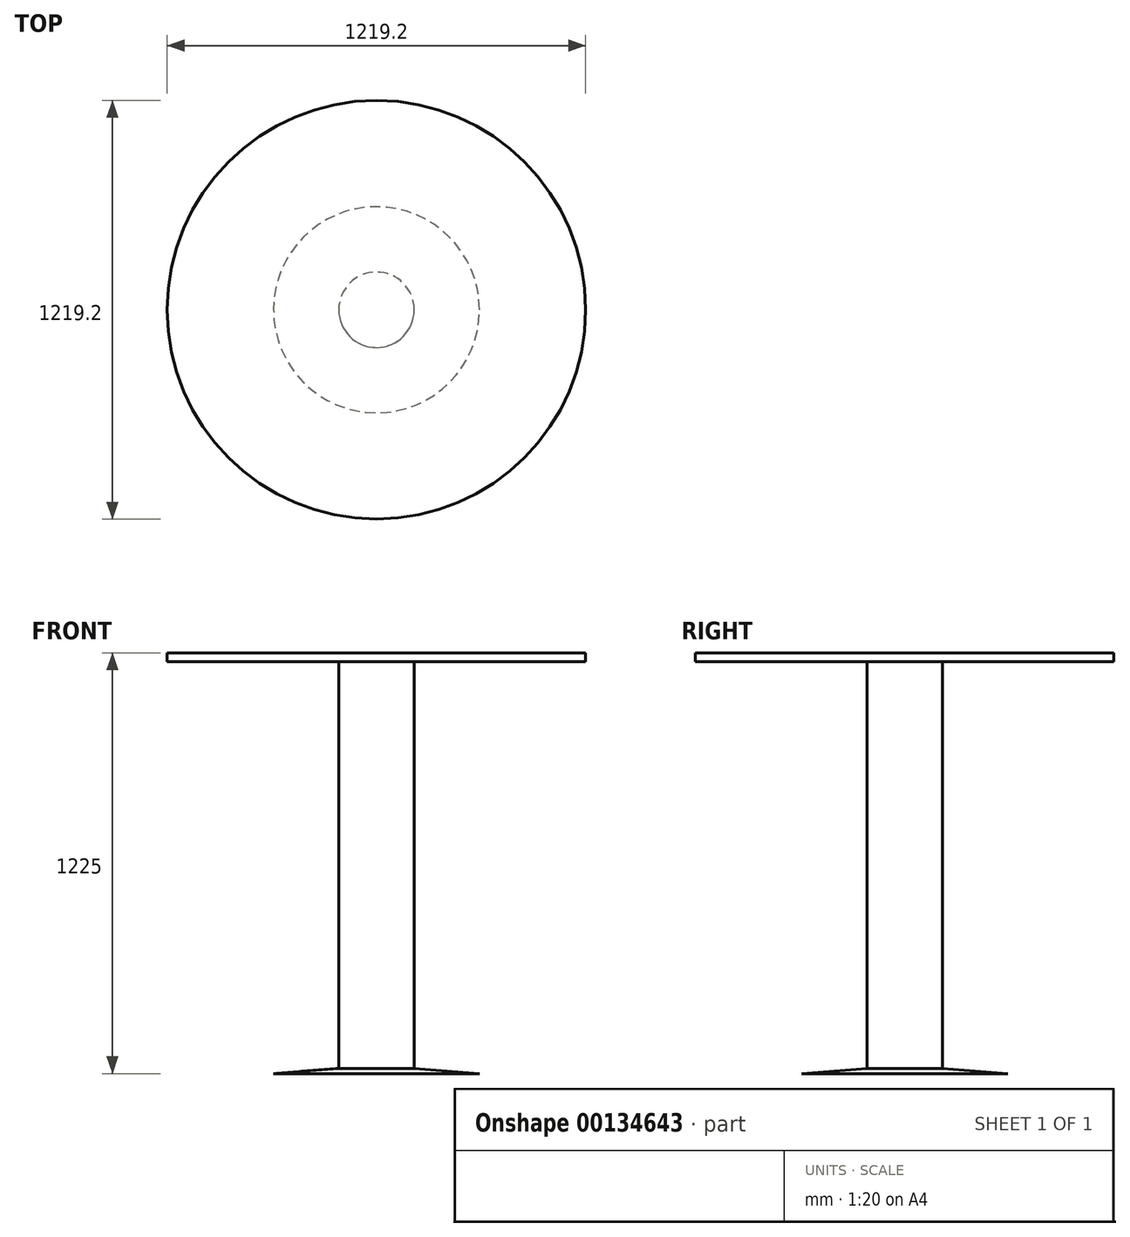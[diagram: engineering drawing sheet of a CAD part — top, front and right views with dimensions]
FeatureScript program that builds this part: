
annotation { "Feature Type Name" : "Feature", "Feature Type Description" : "" }
export const myFeature = defineFeature(function(context is Context, id is Id, definition is map)
    precondition{}
    {
        {
            var Q0;
            Q0=qCreatedBy(makeId("Top.planeOp"),FACE);
            var sketch = newSketch(context, id + "F0", { "sketchPlane" : qUnion([Q0])});
            skCircle(sketch, "E0", {"center": v(0, 0) * mm, "radius": 110 * mm});
            skSolve(sketch);
        }
        {
            var Q0;
            Q0=makeQuery(id+"F0.imprint","IMPRINT",FACE,{"disambiguationData":[TD([[makeQuery(id+"F0.imprint","IMPRINT",EDGE,{"derivedFrom":sQuery(id+"F0.wireOp",EDGE,"E0")}),1.0]])]});
            extrude(context, id + "F1", {"entities" : qUnion([Q0]), "depth" : 1200 * mm});
        }
        {
            var Q0;
            Q0=makeQuery(id+"F1.opExtrude","CAP_FACE",FACE,{"disambiguationData":[OSD([sQuery(id+"F0.wireOp",EDGE,"E0")])],"isStart":false});
            var sketch = newSketch(context, id + "F2", { "sketchPlane" : qUnion([Q0])});
            skCircle(sketch, "E1", {"center": v(0, 0) * mm, "radius": 609.6 * mm});
            skSolve(sketch);
        }
        {
            var Q0;
            Q0=makeQuery(id+"F2.imprint","IMPRINT",FACE,{"disambiguationData":[TD([[makeQuery(id+"F2.imprint","IMPRINT",EDGE,{"derivedFrom":sQuery(id+"F2.wireOp",EDGE,"E1")}),1.0]])]});
            var Q1;
            Q1=makeQuery(id+"F2.imprint","IMPRINT",FACE,{"disambiguationData":[TD([[makeQuery(id+"F2.imprint","IMPRINT",EDGE,{"derivedFrom":makeQuery(id+"F1.opExtrude","CAP_EDGE",EDGE,{"disambiguationData":[OSD([sQuery(id+"F0.wireOp",EDGE,"E0")])],"isStart":false})}),1.0]])]});
            extrude(context, id + "F3", {"entities" : qUnion([Q0, Q1]), "operationType" : NewBodyOperationType.ADD, "depth" : 25 * mm});
        }
        {
            var Q0;
            Q0=makeQuery(id+"F1.opExtrude","CAP_FACE",FACE,{"disambiguationData":[OSD([sQuery(id+"F0.wireOp",EDGE,"E0")])],"isStart":true});
            var sketch = newSketch(context, id + "F4", { "sketchPlane" : qUnion([Q0])});
            skCircle(sketch, "E2", {"center": v(0, 0) * mm, "radius": 300 * mm});
            skSolve(sketch);
        }
        {
            var Q0;
            Q0=makeQuery(id+"F4.imprint","IMPRINT",FACE,{"disambiguationData":[TD([[makeQuery(id+"F4.imprint","IMPRINT",EDGE,{"derivedFrom":sQuery(id+"F4.wireOp",EDGE,"E2")}),1.0]])]});
            var Q1;
            Q1=makeQuery(id+"F4.imprint","IMPRINT",FACE,{"disambiguationData":[TD([[makeQuery(id+"F4.imprint","IMPRINT",EDGE,{"derivedFrom":makeQuery(id+"F1.opExtrude","CAP_EDGE",EDGE,{"disambiguationData":[OSD([sQuery(id+"F0.wireOp",EDGE,"E0")])],"isStart":true})}),-1.0]])]});
            extrude(context, id + "F5", {"entities" : qUnion([Q0, Q1]), "operationType" : NewBodyOperationType.ADD, "oppositeDirection" : true, "depth" : 15 * mm});
        }
        {
            var Q0;
            Q0=makeQuery(id+"F5.opExtrude","CAP_EDGE",EDGE,{"disambiguationData":[OSD([sQuery(id+"F4.wireOp",EDGE,"E2")])],"isStart":false});
            chamfer(context, id + "F6", {"entities" : qUnion([Q0]), "chamferType" : ChamferType.TWO_OFFSETS, "width1" : 15 * mm, "oppositeDirection" : false, "width2" : 190 * mm, "tangentPropagation" : true});
        }
    });
